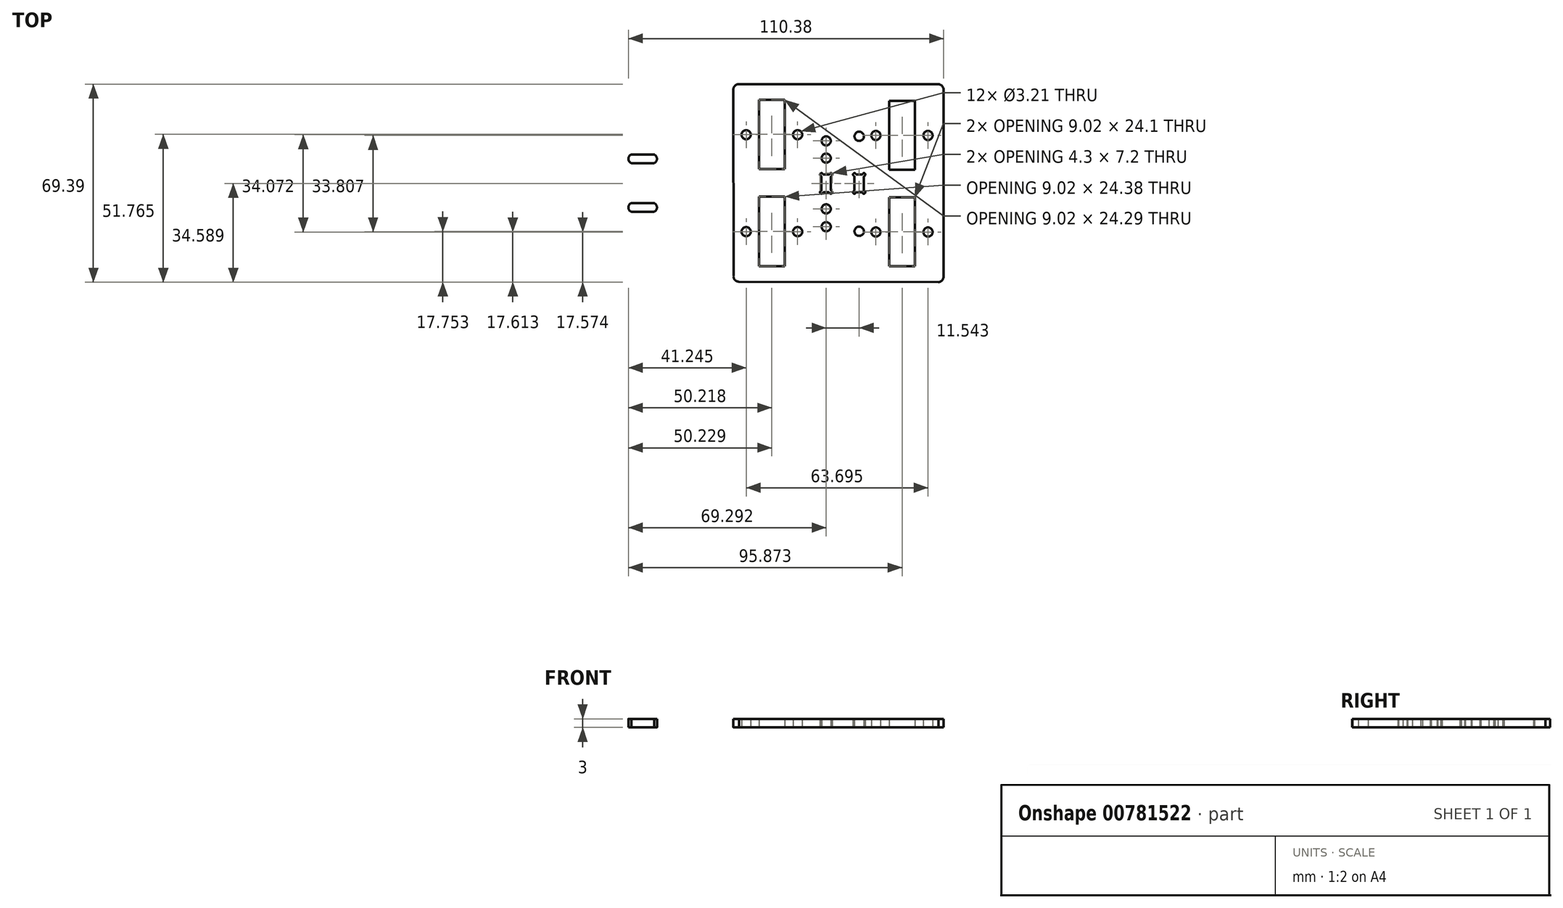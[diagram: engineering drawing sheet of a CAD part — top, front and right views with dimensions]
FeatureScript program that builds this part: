
annotation { "Feature Type Name" : "Feature", "Feature Type Description" : "" }
export const myFeature = defineFeature(function(context is Context, id is Id, definition is map)
    precondition{}
    {
        {
            var Q0;
            Q0=qCreatedBy(makeId("Top.planeOp"),FACE);
            var sketch = newSketch(context, id + "F0", { "sketchPlane" : qUnion([Q0])});
            skLineSegment(sketch, "E0", {"start": v(0.17, 68.15) * mm, "end": v(-7.11, 68.15) * mm});
            skLineSegment(sketch, "E1", {"start": v(-7.99, 67.13) * mm, "end": v(-7.99, 44.73) * mm});
            skLineSegment(sketch, "E2", {"start": v(1.03, 44.73) * mm, "end": v(1.03, 67.13) * mm});
            skLineSegment(sketch, "E3", {"start": v(-7.12, 43.86) * mm, "end": v(0.16, 43.86) * mm});
            skLineSegment(sketch, "E4", {"start": v(-7.12, 34.18) * mm, "end": v(0.16, 34.18) * mm});
            skLineSegment(sketch, "E5", {"start": v(1.04, 33.08) * mm, "end": v(1.04, 10.67) * mm});
            skLineSegment(sketch, "E6", {"start": v(-7.98, 10.67) * mm, "end": v(-7.98, 33.08) * mm});
            skLineSegment(sketch, "E7", {"start": v(0.17, 9.8) * mm, "end": v(-7.11, 9.8) * mm});
            skLineSegment(sketch, "E8", {"start": v(38.52, 33.9) * mm, "end": v(45.8, 33.9) * mm});
            skLineSegment(sketch, "E9", {"start": v(46.68, 33.08) * mm, "end": v(46.68, 10.67) * mm});
            skLineSegment(sketch, "E10", {"start": v(37.67, 10.67) * mm, "end": v(37.67, 33.08) * mm});
            skLineSegment(sketch, "E11", {"start": v(45.81, 9.8) * mm, "end": v(38.53, 9.8) * mm});
            skArc(sketch, "E12", {"start": v(-16.9, 6.38) * mm, "mid": v(-16.35, 4.97) * mm, "end": v(-14.94, 4.42) * mm});
            skArc(sketch, "E13", {"start": v(-14.97, 73.63) * mm, "mid": v(-16.39, 73.04) * mm, "end": v(-16.97, 71.62) * mm});
            skLineSegment(sketch, "E14", {"start": v(-16.97, 71.62) * mm, "end": v(-16.9, 6.38) * mm});
            skCircle(sketch, "E15", {"center": v(27.14, 55.33) * mm, "radius": 1.63 * mm});
            skCircle(sketch, "E16", {"center": v(27.14, 22.06) * mm, "radius": 1.63 * mm});
            skCircle(sketch, "E17", {"center": v(15.6, 23.66) * mm, "radius": 1.6 * mm});
            skCircle(sketch, "E18", {"center": v(15.6, 53.71) * mm, "radius": 1.6 * mm});
            skCircle(sketch, "E19", {"center": v(15.6, 47.68) * mm, "radius": 1.6 * mm});
            skLineSegment(sketch, "E20", {"start": v(25.48, 41.07) * mm, "end": v(25.48, 36.6) * mm});
            skLineSegment(sketch, "E21", {"start": v(28.79, 36.6) * mm, "end": v(28.79, 41.07) * mm});
            skLineSegment(sketch, "E22", {"start": v(26.35, 35.72) * mm, "end": v(27.92, 35.72) * mm});
            skLineSegment(sketch, "E23", {"start": v(27.92, 41.93) * mm, "end": v(26.35, 41.93) * mm});
            skArc(sketch, "E24", {"start": v(25.48, 41.07) * mm, "mid": v(25.42, 41.32) * mm, "end": v(25.23, 41.5) * mm});
            skArc(sketch, "E25", {"start": v(25.23, 36.16) * mm, "mid": v(25.13, 35.37) * mm, "end": v(25.92, 35.47) * mm});
            skArc(sketch, "E26", {"start": v(25.92, 42.18) * mm, "mid": v(25.13, 42.29) * mm, "end": v(25.23, 41.5) * mm});
            skArc(sketch, "E27", {"start": v(25.92, 42.18) * mm, "mid": v(26.1, 42) * mm, "end": v(26.35, 41.93) * mm});
            skArc(sketch, "E28", {"start": v(28.35, 35.47) * mm, "mid": v(28.17, 35.66) * mm, "end": v(27.92, 35.72) * mm});
            skArc(sketch, "E29", {"start": v(28.35, 35.47) * mm, "mid": v(29.14, 35.37) * mm, "end": v(29.04, 36.16) * mm});
            skArc(sketch, "E30", {"start": v(29.04, 41.5) * mm, "mid": v(29.14, 42.29) * mm, "end": v(28.35, 42.18) * mm});
            skArc(sketch, "E31", {"start": v(28.79, 36.6) * mm, "mid": v(28.86, 36.34) * mm, "end": v(29.04, 36.16) * mm});
            skArc(sketch, "E32", {"start": v(25.23, 36.16) * mm, "mid": v(25.42, 36.34) * mm, "end": v(25.48, 36.6) * mm});
            skArc(sketch, "E33", {"start": v(29.04, 41.5) * mm, "mid": v(28.86, 41.32) * mm, "end": v(28.79, 41.07) * mm});
            skArc(sketch, "E34", {"start": v(27.92, 41.93) * mm, "mid": v(28.17, 42) * mm, "end": v(28.35, 42.18) * mm});
            skArc(sketch, "E35", {"start": v(26.35, 35.72) * mm, "mid": v(26.1, 35.66) * mm, "end": v(25.92, 35.47) * mm});
            skCircle(sketch, "E36", {"center": v(15.6, 29.9) * mm, "radius": 1.6 * mm});
            skLineSegment(sketch, "E37", {"start": v(13.94, 41.07) * mm, "end": v(13.94, 36.6) * mm});
            skLineSegment(sketch, "E38", {"start": v(17.24, 36.6) * mm, "end": v(17.24, 41.07) * mm});
            skLineSegment(sketch, "E39", {"start": v(14.8, 35.72) * mm, "end": v(16.38, 35.72) * mm});
            skLineSegment(sketch, "E40", {"start": v(16.38, 41.93) * mm, "end": v(14.8, 41.93) * mm});
            skArc(sketch, "E41", {"start": v(13.94, 41.07) * mm, "mid": v(13.87, 41.32) * mm, "end": v(13.69, 41.5) * mm});
            skArc(sketch, "E42", {"start": v(13.69, 36.16) * mm, "mid": v(13.59, 35.37) * mm, "end": v(14.37, 35.47) * mm});
            skArc(sketch, "E43", {"start": v(14.37, 42.18) * mm, "mid": v(13.59, 42.29) * mm, "end": v(13.69, 41.5) * mm});
            skArc(sketch, "E44", {"start": v(14.37, 42.18) * mm, "mid": v(14.56, 42) * mm, "end": v(14.8, 41.93) * mm});
            skArc(sketch, "E45", {"start": v(16.81, 35.47) * mm, "mid": v(16.63, 35.66) * mm, "end": v(16.38, 35.72) * mm});
            skArc(sketch, "E46", {"start": v(16.81, 35.47) * mm, "mid": v(17.6, 35.37) * mm, "end": v(17.5, 36.16) * mm});
            skArc(sketch, "E47", {"start": v(17.5, 41.5) * mm, "mid": v(17.6, 42.29) * mm, "end": v(16.81, 42.18) * mm});
            skArc(sketch, "E48", {"start": v(17.24, 36.6) * mm, "mid": v(17.31, 36.34) * mm, "end": v(17.5, 36.16) * mm});
            skArc(sketch, "E49", {"start": v(13.69, 36.16) * mm, "mid": v(13.87, 36.34) * mm, "end": v(13.94, 36.6) * mm});
            skArc(sketch, "E50", {"start": v(17.5, 41.5) * mm, "mid": v(17.31, 41.32) * mm, "end": v(17.24, 41.07) * mm});
            skArc(sketch, "E51", {"start": v(16.38, 41.93) * mm, "mid": v(16.63, 42) * mm, "end": v(16.81, 42.18) * mm});
            skArc(sketch, "E52", {"start": v(14.8, 35.72) * mm, "mid": v(14.56, 35.66) * mm, "end": v(14.37, 35.47) * mm});
            skLineSegment(sketch, "E53", {"start": v(-50.32, 20.72) * mm, "end": v(-50.32, 23.95) * mm});
            skLineSegment(sketch, "E54", {"start": v(-47.3, 20.72) * mm, "end": v(-50.32, 20.72) * mm});
            skLineSegment(sketch, "E55", {"start": v(-50.32, 23.95) * mm, "end": v(-47.3, 23.95) * mm});
            skLineSegment(sketch, "E56", {"start": v(-47.3, 25.23) * mm, "end": v(-43.27, 25.23) * mm});
            skLineSegment(sketch, "E57", {"start": v(-43.27, 19.44) * mm, "end": v(-47.3, 19.44) * mm});
            skLineSegment(sketch, "E58", {"start": v(-47.3, 19.44) * mm, "end": v(-47.3, 20.72) * mm});
            skLineSegment(sketch, "E59", {"start": v(-47.3, 23.95) * mm, "end": v(-47.3, 25.23) * mm});
            skLineSegment(sketch, "E60", {"start": v(-43.27, 20.72) * mm, "end": v(-43.27, 19.44) * mm});
            skLineSegment(sketch, "E61", {"start": v(-43.27, 25.23) * mm, "end": v(-43.27, 23.95) * mm});
            skLineSegment(sketch, "E62", {"start": v(-43.27, 20.72) * mm, "end": v(-40.3, 20.72) * mm});
            skLineSegment(sketch, "E63", {"start": v(-43.27, 23.95) * mm, "end": v(-40.31, 23.95) * mm});
            skLineSegment(sketch, "E64", {"start": v(-40.33, 16.44) * mm, "end": v(-55.22, 16.42) * mm});
            skLineSegment(sketch, "E65", {"start": v(-56.66, 60.1) * mm, "end": v(-56.66, 17.85) * mm});
            skLineSegment(sketch, "E66", {"start": v(-39.44, 36.04) * mm, "end": v(-37.8, 36.04) * mm});
            skArc(sketch, "E67", {"start": v(-39.88, 36.3) * mm, "mid": v(-39.7, 36.1) * mm, "end": v(-39.44, 36.04) * mm});
            skArc(sketch, "E68", {"start": v(-39.88, 36.3) * mm, "mid": v(-40.67, 36.4) * mm, "end": v(-40.56, 35.6) * mm});
            skArc(sketch, "E69", {"start": v(-40.31, 35.17) * mm, "mid": v(-40.38, 35.42) * mm, "end": v(-40.56, 35.6) * mm});
            skArc(sketch, "E70", {"start": v(-37.8, 36.04) * mm, "mid": v(-37.45, 36.19) * mm, "end": v(-37.3, 36.54) * mm});
            skLineSegment(sketch, "E71", {"start": v(-37.3, 36.54) * mm, "end": v(-37.31, 41.14) * mm});
            skLineSegment(sketch, "E72", {"start": v(-39.44, 41.64) * mm, "end": v(-37.8, 41.64) * mm});
            skArc(sketch, "E73", {"start": v(-40.56, 42.08) * mm, "mid": v(-40.38, 42.26) * mm, "end": v(-40.31, 42.51) * mm});
            skArc(sketch, "E74", {"start": v(-40.56, 42.08) * mm, "mid": v(-40.67, 41.3) * mm, "end": v(-39.88, 41.4) * mm});
            skArc(sketch, "E75", {"start": v(-39.44, 41.64) * mm, "mid": v(-39.7, 41.58) * mm, "end": v(-39.88, 41.4) * mm});
            skArc(sketch, "E76", {"start": v(-37.3, 41.14) * mm, "mid": v(-37.45, 41.5) * mm, "end": v(-37.8, 41.64) * mm});
            skLineSegment(sketch, "E77", {"start": v(-40.33, 61.5) * mm, "end": v(-55.22, 61.52) * mm});
            skArc(sketch, "E78", {"start": v(-56.66, 17.85) * mm, "mid": v(-56.3, 16.77) * mm, "end": v(-55.22, 16.42) * mm});
            skArc(sketch, "E79", {"start": v(-55.22, 61.52) * mm, "mid": v(-56.3, 61.17) * mm, "end": v(-56.66, 60.1) * mm});
            skLineSegment(sketch, "E80", {"start": v(-44.69, 48.94) * mm, "end": v(-52.7, 48.94) * mm});
            skLineSegment(sketch, "E81", {"start": v(-44.69, 45.94) * mm, "end": v(-52.7, 45.94) * mm});
            skLineSegment(sketch, "E82", {"start": v(-44.69, 31.92) * mm, "end": v(-52.7, 31.92) * mm});
            skLineSegment(sketch, "E83", {"start": v(-44.69, 28.91) * mm, "end": v(-52.7, 28.91) * mm});
            skArc(sketch, "E84", {"start": v(-44.69, 28.91) * mm, "mid": v(-43.69, 30.41) * mm, "end": v(-44.69, 31.92) * mm});
            skArc(sketch, "E85", {"start": v(-52.7, 31.92) * mm, "mid": v(-53.7, 30.41) * mm, "end": v(-52.7, 28.91) * mm});
            skArc(sketch, "E86", {"start": v(-44.69, 45.94) * mm, "mid": v(-43.69, 47.44) * mm, "end": v(-44.69, 48.94) * mm});
            skArc(sketch, "E87", {"start": v(-52.7, 48.94) * mm, "mid": v(-53.7, 47.44) * mm, "end": v(-52.7, 45.94) * mm});
            skLineSegment(sketch, "E88", {"start": v(-40.31, 42.51) * mm, "end": v(-40.32, 54) * mm});
            skLineSegment(sketch, "E89", {"start": v(-40.33, 57.22) * mm, "end": v(-40.33, 61.5) * mm});
            skLineSegment(sketch, "E90", {"start": v(-40.31, 35.17) * mm, "end": v(-40.32, 23.95) * mm});
            skLineSegment(sketch, "E91", {"start": v(-40.33, 20.72) * mm, "end": v(-40.33, 16.44) * mm});
            skLineSegment(sketch, "E92", {"start": v(-50.32, 57.22) * mm, "end": v(-50.32, 54) * mm});
            skLineSegment(sketch, "E93", {"start": v(-47.3, 57.22) * mm, "end": v(-50.32, 57.22) * mm});
            skLineSegment(sketch, "E94", {"start": v(-50.32, 54) * mm, "end": v(-47.3, 54) * mm});
            skLineSegment(sketch, "E95", {"start": v(-47.3, 52.71) * mm, "end": v(-43.27, 52.71) * mm});
            skLineSegment(sketch, "E96", {"start": v(-43.27, 58.5) * mm, "end": v(-47.3, 58.5) * mm});
            skLineSegment(sketch, "E97", {"start": v(-47.3, 58.5) * mm, "end": v(-47.3, 57.22) * mm});
            skLineSegment(sketch, "E98", {"start": v(-47.3, 54) * mm, "end": v(-47.3, 52.71) * mm});
            skLineSegment(sketch, "E99", {"start": v(-43.27, 57.22) * mm, "end": v(-43.27, 58.5) * mm});
            skLineSegment(sketch, "E100", {"start": v(-43.27, 52.71) * mm, "end": v(-43.27, 54) * mm});
            skLineSegment(sketch, "E101", {"start": v(-43.27, 57.22) * mm, "end": v(-40.3, 57.22) * mm});
            skLineSegment(sketch, "E102", {"start": v(-43.27, 54) * mm, "end": v(-40.31, 54) * mm});
            skArc(sketch, "E103", {"start": v(54.97, 4.24) * mm, "mid": v(56.2, 4.91) * mm, "end": v(56.68, 6.22) * mm});
            skPoint(sketch, "E104.orphan", {"position": v(56.68, 4.24) * mm});
            skArc(sketch, "E105", {"start": v(56.68, 71.92) * mm, "mid": v(56, 73.14) * mm, "end": v(54.7, 73.63) * mm});
            skPoint(sketch, "E106.orphan", {"position": v(56.68, 73.63) * mm});
            skLineSegment(sketch, "E107", {"start": v(38.52, 67.71) * mm, "end": v(45.8, 67.71) * mm});
            skLineSegment(sketch, "E108", {"start": v(46.68, 66.88) * mm, "end": v(46.68, 44.48) * mm});
            skLineSegment(sketch, "E109", {"start": v(37.67, 44.48) * mm, "end": v(37.67, 66.88) * mm});
            skLineSegment(sketch, "E110", {"start": v(45.81, 43.6) * mm, "end": v(38.53, 43.6) * mm});
            skCircle(sketch, "E111", {"center": v(51.24, 21.81) * mm, "radius": 1.6 * mm});
            skCircle(sketch, "E112", {"center": v(33, 21.81) * mm, "radius": 1.6 * mm});
            skCircle(sketch, "E113", {"center": v(5.58, 21.94) * mm, "radius": 1.6 * mm});
            skCircle(sketch, "E114", {"center": v(-12.46, 21.94) * mm, "radius": 1.6 * mm});
            skCircle(sketch, "E115", {"center": v(-12.46, 55.89) * mm, "radius": 1.6 * mm});
            skCircle(sketch, "E116", {"center": v(5.58, 55.89) * mm, "radius": 1.6 * mm});
            skCircle(sketch, "E117", {"center": v(33, 55.62) * mm, "radius": 1.6 * mm});
            skCircle(sketch, "E118", {"center": v(51.24, 55.62) * mm, "radius": 1.6 * mm});
            skLineSegment(sketch, "E119", {"start": v(-7.98, 10.67) * mm, "end": v(-7.98, 9.8) * mm});
            skLineSegment(sketch, "E120", {"start": v(-7.98, 9.8) * mm, "end": v(-7.11, 9.8) * mm});
            skLineSegment(sketch, "E121", {"start": v(0.17, 9.8) * mm, "end": v(1.04, 9.8) * mm});
            skLineSegment(sketch, "E122", {"start": v(1.04, 10.67) * mm, "end": v(1.04, 9.8) * mm});
            skLineSegment(sketch, "E123", {"start": v(-7.98, 33.08) * mm, "end": v(-7.98, 34.18) * mm});
            skLineSegment(sketch, "E124", {"start": v(-7.98, 34.18) * mm, "end": v(-7.12, 34.18) * mm});
            skLineSegment(sketch, "E125", {"start": v(0.16, 34.18) * mm, "end": v(1.04, 34.18) * mm});
            skLineSegment(sketch, "E126", {"start": v(1.04, 34.18) * mm, "end": v(1.04, 33.08) * mm});
            skLineSegment(sketch, "E127", {"start": v(0.16, 43.86) * mm, "end": v(1.03, 43.86) * mm});
            skLineSegment(sketch, "E128", {"start": v(1.03, 44.73) * mm, "end": v(1.03, 43.86) * mm});
            skLineSegment(sketch, "E129", {"start": v(-7.99, 44.73) * mm, "end": v(-7.99, 43.86) * mm});
            skLineSegment(sketch, "E130", {"start": v(-7.12, 43.86) * mm, "end": v(-7.99, 43.86) * mm});
            skLineSegment(sketch, "E131", {"start": v(-7.11, 68.15) * mm, "end": v(-7.99, 68.15) * mm});
            skLineSegment(sketch, "E132", {"start": v(-7.99, 68.15) * mm, "end": v(-7.99, 67.13) * mm});
            skLineSegment(sketch, "E133", {"start": v(1.03, 67.13) * mm, "end": v(1.03, 68.15) * mm});
            skLineSegment(sketch, "E134", {"start": v(1.03, 68.15) * mm, "end": v(0.17, 68.15) * mm});
            skLineSegment(sketch, "E135", {"start": v(38.52, 67.71) * mm, "end": v(37.67, 67.71) * mm});
            skLineSegment(sketch, "E136", {"start": v(37.67, 67.71) * mm, "end": v(37.67, 66.88) * mm});
            skLineSegment(sketch, "E137", {"start": v(45.8, 67.71) * mm, "end": v(46.68, 67.71) * mm});
            skLineSegment(sketch, "E138", {"start": v(46.68, 67.71) * mm, "end": v(46.68, 66.88) * mm});
            skLineSegment(sketch, "E139", {"start": v(46.68, 44.48) * mm, "end": v(46.68, 43.6) * mm});
            skLineSegment(sketch, "E140", {"start": v(45.81, 43.6) * mm, "end": v(46.68, 43.6) * mm});
            skLineSegment(sketch, "E141", {"start": v(38.53, 43.6) * mm, "end": v(37.67, 43.6) * mm});
            skLineSegment(sketch, "E142", {"start": v(37.67, 44.48) * mm, "end": v(37.67, 43.6) * mm});
            skLineSegment(sketch, "E143", {"start": v(38.53, 9.8) * mm, "end": v(37.67, 9.8) * mm});
            skLineSegment(sketch, "E144", {"start": v(37.67, 10.67) * mm, "end": v(37.67, 9.8) * mm});
            skLineSegment(sketch, "E145", {"start": v(45.81, 9.8) * mm, "end": v(46.68, 9.8) * mm});
            skLineSegment(sketch, "E146", {"start": v(46.68, 10.67) * mm, "end": v(46.68, 9.8) * mm});
            skLineSegment(sketch, "E147", {"start": v(37.67, 33.08) * mm, "end": v(37.67, 33.9) * mm});
            skLineSegment(sketch, "E148", {"start": v(37.67, 33.9) * mm, "end": v(38.52, 33.9) * mm});
            skLineSegment(sketch, "E149", {"start": v(45.8, 33.9) * mm, "end": v(46.68, 33.9) * mm});
            skLineSegment(sketch, "E150", {"start": v(46.68, 33.9) * mm, "end": v(46.68, 33.08) * mm});
            skLineSegment(sketch, "E151", {"start": v(56.68, 71.92) * mm, "end": v(56.68, 6.22) * mm});
            skLineSegment(sketch, "E152", {"start": v(-14.97, 73.63) * mm, "end": v(54.7, 73.63) * mm});
            skLineSegment(sketch, "E153", {"start": v(-14.94, 4.42) * mm, "end": v(54.97, 4.24) * mm});
            skSolve(sketch);
        }
        {
            var Q0;
            Q0 = qSketchRegion(id + "F0", true);
            extrude(context, id + "F1", {"entities" : qUnion([Q0]), "depth" : 3 * mm, "offsetDistance" : 25 * mm});
        }
    });
